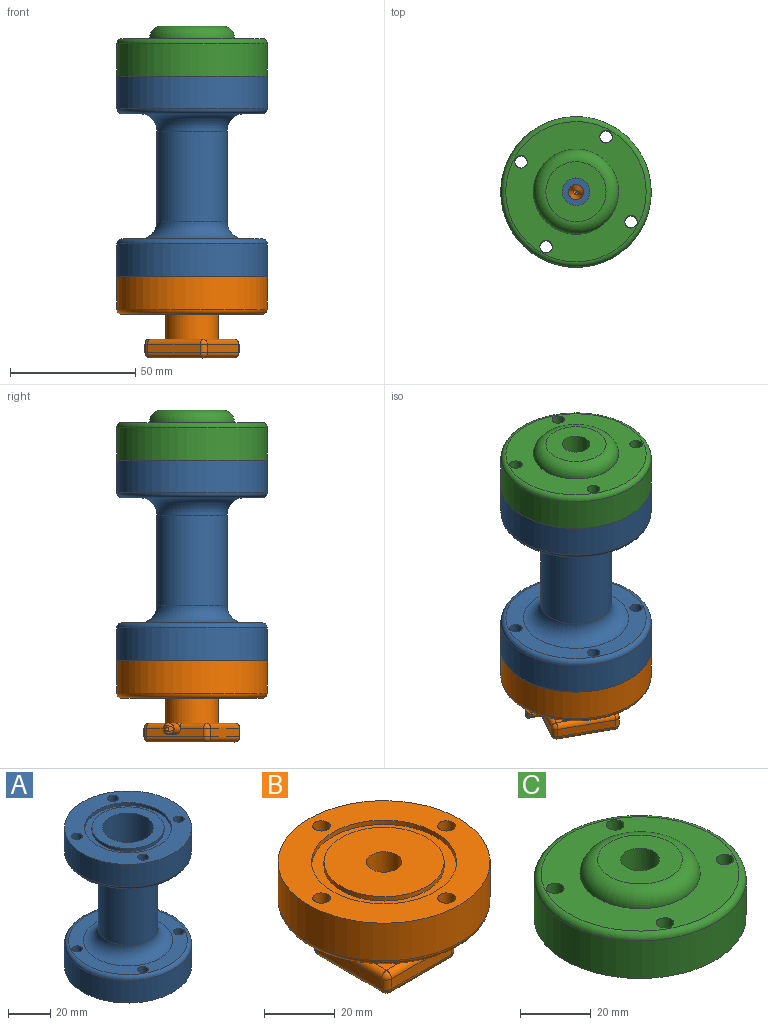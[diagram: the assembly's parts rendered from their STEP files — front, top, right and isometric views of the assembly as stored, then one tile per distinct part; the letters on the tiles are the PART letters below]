
ASSEMBLY  parts=3 mates=5
PART A: 32 faces, bbox 64.9x64.9x80 mm
  f0: plane 34x34mm, normal (0,0,1), area 455.5mm2, adj f10,f29
  f1: cylinder r=2.5mm len=15mm, axis (0,0,-1), area 235.6mm2, adj f9,f23
  f2: cylinder r=2.5mm len=15mm, axis (0,0,-1), area 235.6mm2, adj f9,f23
  f3: cylinder r=2.5mm len=15mm, axis (0,0,-1), area 235.6mm2, adj f9,f23
  f4: cylinder r=2.5mm len=15mm, axis (0,0,-1), area 235.6mm2, adj f9,f23
  f5: cylinder r=30mm len=60mm, axis (0,0,-1), area 2450.4mm2, adj f9,f28
  f6: plane 34x34mm, normal (0,0,-1), area 879.6mm2, adj f17,f21
  f7: cylinder r=11mm len=35mm, axis (0,0,-1), area 2419mm2, adj f8,f20
  f8: plane 24x24mm, normal (0,0,1), area 72.3mm2, adj f7,f10
  f9: plane 60x60mm, normal (0,0,-1), area 1428.6mm2, adj f1,f2,f3,f4,f5,f18
  f10: cylinder r=12mm len=40mm, axis (0,0,-1), area 3015.9mm2, adj f0,f8
  f11: plane 60x60mm, normal (0,0,1), area 1428.6mm2, adj f12,f13,f14,f15,f16,f30
  f12: cylinder r=2.5mm len=15mm, axis (0,0,-1), area 235.6mm2, adj f11,f24
  f13: cylinder r=2.5mm len=15mm, axis (0,0,-1), area 235.6mm2, adj f11,f24
  f14: cylinder r=2.5mm len=15mm, axis (0,0,-1), area 235.6mm2, adj f11,f24
  f15: cylinder r=2.5mm len=15mm, axis (0,0,-1), area 235.6mm2, adj f11,f24
  f16: cylinder r=30mm len=60mm, axis (0,0,-1), area 2450.4mm2, adj f11,f27
  f17: cylinder r=17mm len=34mm, axis (0,0,-1), area 186.9mm2, adj f6,f19
  f18: cylinder r=20.5mm len=41mm, axis (0,0,-1), area 225.4mm2, adj f9,f19
  f19: plane 41x41mm, normal (0,0,-1), area 412.3mm2, adj f17,f18
  f20: plane 22x22mm, normal (0,0,1), area 351.9mm2, adj f7,f21
  f21: cylinder r=3mm len=6mm, axis (0,0,-1), area 94.2mm2, adj f6,f20
  f22: cylinder r=14mm len=36mm, axis (0,0,1), area 3166.7mm2, adj f25,f26
  f23: plane 56x56mm, normal (0,0,1), area 999mm2, adj f1,f2,f3,f4,f26,f28
  f24: plane 56x56mm, normal (0,0,-1), area 999mm2, adj f12,f13,f14,f15,f25,f27
  f25: torus R=21mm, axis (0,0,1), area 1143mm2, adj f22,f24
  f26: torus R=21mm, axis (0,0,1), area 1143mm2, adj f22,f23
  f27: torus R=28mm, axis (0,0,1), area 577.8mm2, adj f16,f24
  f28: torus R=28mm, axis (0,0,1), area 577.8mm2, adj f5,f23
  f29: cylinder r=17mm len=34mm, axis (0,0,1), area 186.9mm2, adj f0,f31
  f30: cylinder r=20.5mm len=41mm, axis (0,0,1), area 225.4mm2, adj f11,f31
  f31: plane 41x41mm, normal (0,0,1), area 412.3mm2, adj f29,f30
PART B: 68 faces, bbox 64.9x64.9x32.5 mm
  f0: plane 0.64x0.05mm, normal (0,0,1), area 0mm2, adj f4,f31,f32,f33
  f1: plane 34x34mm, normal (0,0,1), area 829.4mm2, adj f2,f11
  f2: cylinder r=5mm len=10mm, axis (0,0,1), area 251.3mm2, adj f1,f3
  f3: plane 10x10mm, normal (0,0,1), area 40.1mm2, adj f2,f4
  f4: cone r=3.5mm half-angle=8.4deg, axis (0,0,1), area 242.9mm2, adj f0,f3,f12,f30,f34,f35,f38
  f5: cylinder r=10.5mm len=21mm, axis (0,0,1), area 659.7mm2, adj f6,f13
  f6: plane 56x56mm, normal (0,0,-1), area 2038.1mm2, adj f5,f63,f64,f65,f66,f67
  f7: cylinder r=30mm len=60mm, axis (0,0,1), area 2450.4mm2, adj f8,f63
  f8: plane 60x60mm, normal (0,0,1), area 1428.6mm2, adj f7,f9,f64,f65,f66,f67
  f9: cylinder r=20.5mm len=41mm, axis (0,0,1), area 193.2mm2, adj f8,f10
  f10: plane 41x41mm, normal (0,0,1), area 412.3mm2, adj f9,f11
  f11: cylinder r=17mm len=34mm, axis (0,0,1), area 160.2mm2, adj f1,f10
  f12: plane 0.64x0.05mm, normal (0,0,1), area 0mm2, adj f4,f36,f37,f39
  f13: plane 26x26mm, normal (0,0,1), area 280mm2, adj f5,f41,f43,f44,f45,f46,f47,f59
  f14: plane 26x3.5mm, normal (-1,0,0), area 91mm2, adj f55,f58,f59,f62
  f15: plane 26x24mm, normal (0,0,-1), area 624mm2, adj f40,f42,f54,f58
  f16: plane 26x3.5mm, normal (1,0,0), area 81.9mm2, adj f21,f46,f47,f50,f51,f54
  f17: plane 24x3.5mm, normal (0,-1,0), area 84mm2, adj f42,f43,f50,f62
  f18: plane 24x3.5mm, normal (0,1,0), area 84mm2, adj f40,f41,f51,f55
  f19: plane 2.25x2.05mm, normal (0,-1,0), area 1.7mm2, adj f25,f26,f27,f28,f29,f32
  f20: plane 2.25x2.05mm, normal (0,1,0), area 1.7mm2, adj f25,f26,f27,f28,f29,f37
  f21: cylinder r=2.25mm len=6mm, axis (1,0,0), area 78.4mm2, adj f16,f22,f23,f44,f45
  f22: bspline ~4.5x2.25mm, area 7.5mm2, adj f21,f24
  f23: bspline ~4.5x2.25mm, area 7.5mm2, adj f21,f24
  f24: cylinder r=2.25mm len=4.5mm, axis (0,0,-1), area 9.5mm2, adj f22,f23,f27
  f25: cylinder r=0.75mm len=2mm, axis (0,0,-1), area 4.4mm2, adj f19,f20,f26,f33,f34,f38,f39
  f26: torus R=0.25mm, axis (0,-1,0), area 2.7mm2, adj f19,f20,f25,f27
  f27: cylinder r=0.75mm len=21mm, axis (1,0,0), area 93.9mm2, adj f19,f20,f24,f26,f28
  f28: torus R=1.75mm, axis (0,-1,0), area 4.7mm2, adj f19,f20,f27,f29
  f29: cylinder r=0.75mm len=1.5mm, axis (0,0,1), area 0.9mm2, adj f19,f20,f28,f30,f31,f35,f36
  f30: bspline ~0.96x0.72mm, area 0.2mm2, adj f4,f29,f31
  f31: torus R=0.95mm, axis (0,0,1), area 0mm2, adj f0,f29,f30,f32
  f32: cylinder r=0.2mm len=0.5mm, axis (1,0,0), area 0.2mm2, adj f0,f19,f31,f33
  f33: torus R=0.95mm, axis (0,0,1), area 0mm2, adj f0,f25,f32,f34
  f34: bspline ~0.95x0.69mm, area 0.2mm2, adj f4,f25,f33
  f35: bspline ~0.96x0.72mm, area 0.2mm2, adj f4,f29,f36
  f36: torus R=0.95mm, axis (0,0,1), area 0mm2, adj f12,f29,f35,f37
  f37: cylinder r=0.2mm len=0.5mm, axis (-1,0,0), area 0.2mm2, adj f12,f20,f36,f39
  f38: bspline ~0.96x0.72mm, area 0.2mm2, adj f4,f25,f39
  f39: torus R=0.95mm, axis (0,0,1), area 0mm2, adj f12,f25,f37,f38
  f40: cylinder r=2mm len=24mm, axis (1,0,0), area 75.4mm2, adj f15,f18,f53,f56
  f41: cylinder r=2mm len=24mm, axis (-1,0,0), area 75.4mm2, adj f13,f18,f49,f57
  f42: cylinder r=2mm len=24mm, axis (-1,0,0), area 75.4mm2, adj f15,f17,f52,f60
  f43: cylinder r=2mm len=24mm, axis (1,0,0), area 75.4mm2, adj f13,f17,f48,f61
  f44: bspline ~2.46x2.03mm, area 3.8mm2, adj f13,f21,f46
  f45: bspline ~2.46x2.03mm, area 3.8mm2, adj f13,f21,f47
  f46: cylinder r=2mm len=10.76mm, axis (0,1,0), area 33.8mm2, adj f13,f16,f44,f48
  f47: cylinder r=2mm len=10.76mm, axis (0,1,0), area 33.8mm2, adj f13,f16,f45,f49
  f48: sphere r=2mm, area 6.3mm2, adj f43,f46,f50
  f49: sphere r=2mm, area 6.3mm2, adj f41,f47,f51
  f50: cylinder r=2mm len=3.5mm, axis (0,0,-1), area 11mm2, adj f16,f17,f48,f52
  f51: cylinder r=2mm len=3.5mm, axis (0,0,1), area 11mm2, adj f16,f18,f49,f53
  f52: sphere r=2mm, area 6.3mm2, adj f42,f50,f54
  f53: sphere r=2mm, area 6.3mm2, adj f40,f51,f54
  f54: cylinder r=2mm len=26mm, axis (0,1,0), area 81.7mm2, adj f15,f16,f52,f53
  f55: cylinder r=2mm len=3.5mm, axis (0,0,-1), area 11mm2, adj f14,f18,f56,f57
  f56: sphere r=2mm, area 6.3mm2, adj f40,f55,f58
  f57: sphere r=2mm, area 6.3mm2, adj f41,f55,f59
  f58: cylinder r=2mm len=26mm, axis (0,1,0), area 81.7mm2, adj f14,f15,f56,f60
  f59: cylinder r=2mm len=26mm, axis (0,1,0), area 81.7mm2, adj f13,f14,f57,f61
  f60: sphere r=2mm, area 6.3mm2, adj f42,f58,f62
  f61: sphere r=2mm, area 6.3mm2, adj f43,f59,f62
  f62: cylinder r=2mm len=3.5mm, axis (0,0,1), area 11mm2, adj f14,f17,f60,f61
  f63: torus R=28mm, axis (0,0,1), area 577.8mm2, adj f6,f7
  f64: cylinder r=2.5mm len=15mm, axis (0,0,1), area 235.6mm2, adj f6,f8
  f65: cylinder r=2.5mm len=15mm, axis (0,0,1), area 235.6mm2, adj f6,f8
  f66: cylinder r=2.5mm len=15mm, axis (0,0,1), area 235.6mm2, adj f6,f8
  f67: cylinder r=2.5mm len=15mm, axis (0,0,1), area 235.6mm2, adj f6,f8
PART C: 15 faces, bbox 64.9x64.9x20 mm
  f0: plane 34x34mm, normal (0,0,-1), area 812.9mm2, adj f8,f11
  f1: plane 56x56mm, normal (0,0,1), area 1476.5mm2, adj f3,f4,f5,f6,f13,f14
  f2: plane 60x60mm, normal (0,0,-1), area 1428.6mm2, adj f3,f4,f5,f6,f7,f9
  f3: cylinder r=2.5mm len=15mm, axis (0,0,-1), area 235.6mm2, adj f1,f2
  f4: cylinder r=2.5mm len=15mm, axis (0,0,-1), area 235.6mm2, adj f1,f2
  f5: cylinder r=2.5mm len=15mm, axis (0,0,-1), area 235.6mm2, adj f1,f2
  f6: cylinder r=2.5mm len=15mm, axis (0,0,-1), area 235.6mm2, adj f1,f2
  f7: cylinder r=30mm len=60mm, axis (0,0,-1), area 2450.4mm2, adj f2,f13
  f8: cylinder r=17mm len=34mm, axis (0,0,-1), area 186.9mm2, adj f0,f10
  f9: cylinder r=20.5mm len=41mm, axis (0,0,-1), area 225.4mm2, adj f2,f10
  f10: plane 41x41mm, normal (0,0,-1), area 412.3mm2, adj f8,f9
  f11: cylinder r=5.5mm len=20mm, axis (0,0,-1), area 691.2mm2, adj f0,f12
  f12: plane 24x24mm, normal (0,0,1), area 357.4mm2, adj f11,f14
  f13: torus R=28mm, axis (0,0,1), area 577.8mm2, adj f1,f7
  f14: torus R=12mm, axis (0,0,1), area 749.3mm2, adj f1,f12
PLACE A t=(67.59,21.57,-131.52)mm
PLACE B rot(axis=(0,0,1),151.4deg) t=(67.59,21.57,-131.52)mm
PLACE C rot(axis=(0.31,0.39,0.87),0deg) t=(67.59,21.57,-51.52)mm
MATE cylindrical C.f3 <-> A.f1  axis (0,0,-1) through (55.62,-0.38,-51.52)mm
MATE cylindrical B.f67 <-> A.f2  axis (0,0,1) through (89.54,9.6,-131.52)mm
MATE planar B.f2 <-> A.f4  axis (0,0,1) through (67.59,21.57,-131.52)mm
MATE planar C.f5 <-> A.f3  axis (0,0,-1) through (79.56,43.52,-51.52)mm
MATE cylindrical B.f65 <-> A.f4  axis (0,0,1) through (45.64,33.54,-131.52)mm
